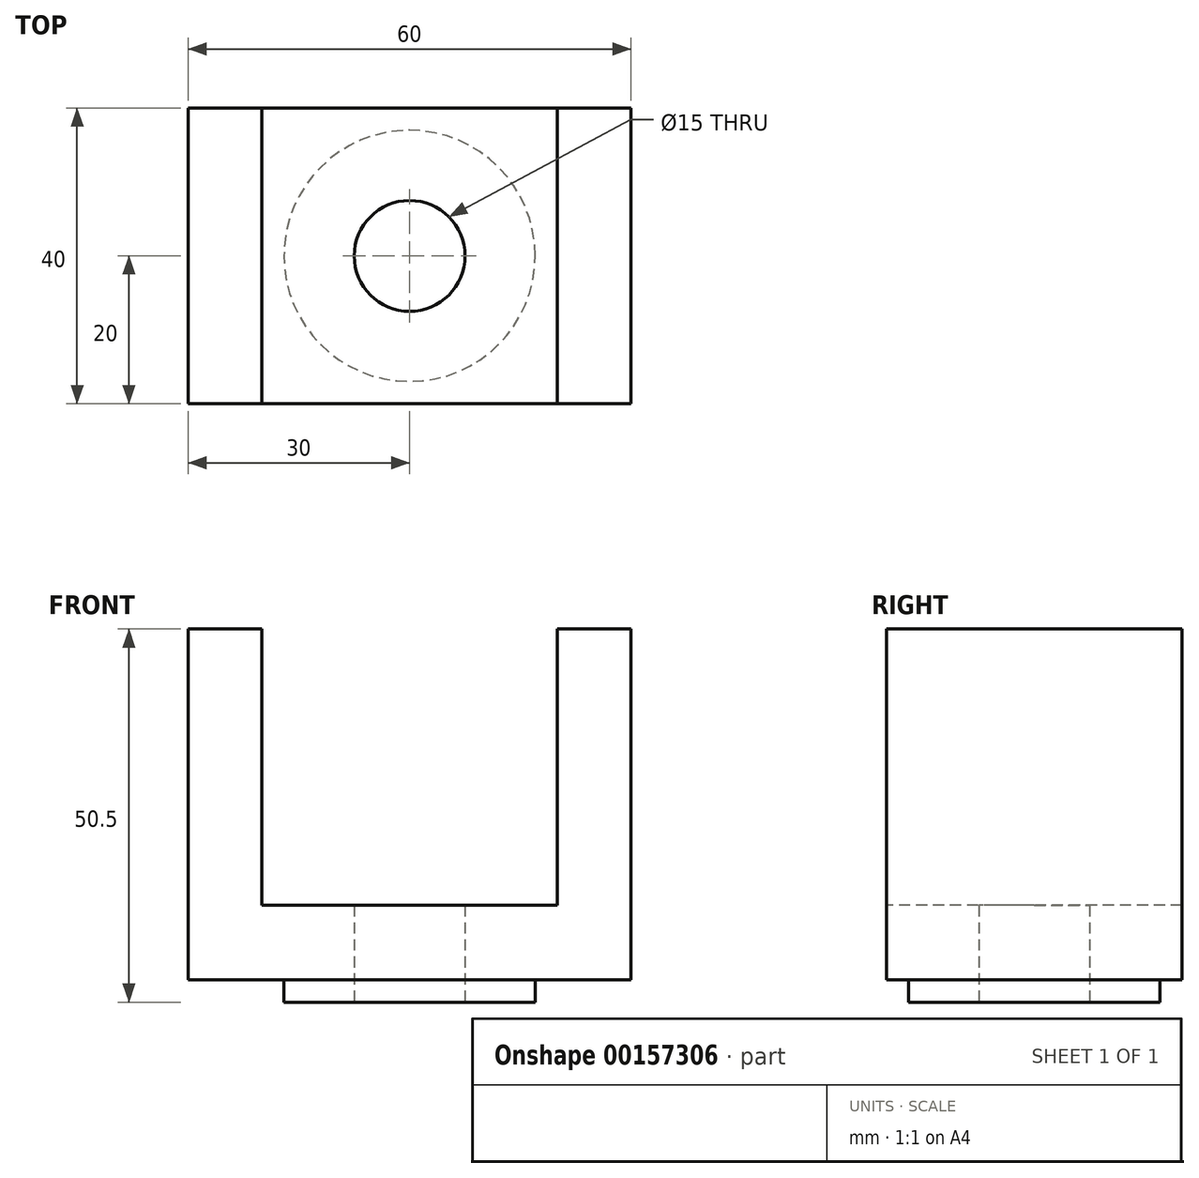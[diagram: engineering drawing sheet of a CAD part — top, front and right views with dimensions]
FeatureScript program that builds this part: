
annotation { "Feature Type Name" : "Feature", "Feature Type Description" : "" }
export const myFeature = defineFeature(function(context is Context, id is Id, definition is map)
    precondition{}
    {
        {
            var Q0;
            Q0=qCreatedBy(makeId("Top.planeOp"),FACE);
            var sketch = newSketch(context, id + "F0", { "sketchPlane" : qUnion([Q0])});
            skLineSegment(sketch, "E0", {"start": v(0, 0) * mm, "end": v(60, 0) * mm});
            skLineSegment(sketch, "E1", {"start": v(60, 0) * mm, "end": v(60, -40) * mm});
            skLineSegment(sketch, "E2", {"start": v(60, -40) * mm, "end": v(0, -40) * mm});
            skLineSegment(sketch, "E3", {"start": v(0, -40) * mm, "end": v(0, 0) * mm});
            skSolve(sketch);
        }
        {
            var Q0;
            Q0 = qSketchRegion(id + "F0", true);
            extrude(context, id + "F1", {"entities" : qUnion([Q0]), "depth" : 50.5 * mm});
        }
        {
            var Q0;
            Q0=makeQuery(id+"F1.opExtrude","SWEPT_FACE",FACE,{"disambiguationData":[OSD([sQuery(id+"F0.wireOp",EDGE,"E2")])]});
            var sketch = newSketch(context, id + "F2", { "sketchPlane" : qUnion([Q0])});
            skLineSegment(sketch, "E4", {"start": v(0, 0) * mm, "end": v(0, 3) * mm});
            skLineSegment(sketch, "E5", {"start": v(0, 3) * mm, "end": v(60, 3) * mm});
            skLineSegment(sketch, "E6", {"start": v(60, 3) * mm, "end": v(60, 0) * mm});
            skLineSegment(sketch, "E7", {"start": v(60, 0) * mm, "end": v(0, 0) * mm});
            skSolve(sketch);
        }
        {
            var Q0;
            Q0 = qSketchRegion(id + "F2", true);
            extrude(context, id + "F3", {"entities" : qUnion([Q0]), "operationType" : NewBodyOperationType.REMOVE, "endBound" : BoundingType.THROUGH_ALL, "oppositeDirection" : true, "depth" : 25 * mm});
        }
        {
            var Q0;
            Q0=makeQuery(id+"F3.boolean.opBoolean","COPY",FACE,{"derivedFrom":makeQuery(id+"F3.opExtrude","SWEPT_FACE",FACE,{"disambiguationData":[OSD([sQuery(id+"F2.wireOp",EDGE,"E5")])]})});
            var sketch = newSketch(context, id + "F4", { "sketchPlane" : qUnion([Q0])});
            skLineSegment(sketch, "E8", {"start": v(0, 0) * mm, "end": v(60, 0) * mm});
            skCircle(sketch, "E9", {"center": v(30, 20) * mm, "radius": 17 * mm});
            skSolve(sketch);
        }
        {
            var Q0;
            Q0 = qSketchRegion(id + "F4", true);
            extrude(context, id + "F5", {"entities" : qUnion([Q0]), "operationType" : NewBodyOperationType.ADD, "depth" : 3 * mm});
        }
        {
            var Q0;
            Q0=makeQuery(id+"F1.opExtrude","SWEPT_FACE",FACE,{"disambiguationData":[OSD([sQuery(id+"F0.wireOp",EDGE,"E2")])]});
            var sketch = newSketch(context, id + "F6", { "sketchPlane" : qUnion([Q0])});
            skLineSegment(sketch, "E10", {"start": v(0, 3) * mm, "end": v(0, 50.5) * mm});
            skLineSegment(sketch, "E11", {"start": v(0, 50.5) * mm, "end": v(10, 50.5) * mm});
            skLineSegment(sketch, "E12", {"start": v(10, 50.5) * mm, "end": v(10, 13.1) * mm});
            skLineSegment(sketch, "E13", {"start": v(50, 13.1) * mm, "end": v(50, 50.5) * mm});
            skLineSegment(sketch, "E14", {"start": v(50, 50.5) * mm, "end": v(60, 50.5) * mm});
            skLineSegment(sketch, "E15", {"start": v(50, 13.1) * mm, "end": v(10, 13.1) * mm});
            skLineSegment(sketch, "E16", {"start": v(60, 50.5) * mm, "end": v(60, 3) * mm});
            skLineSegment(sketch, "E17", {"start": v(60, 3) * mm, "end": v(0, 3) * mm});
            skSolve(sketch);
        }
        {
            var Q0;
            {var subQ0=sQuery(id+"F6.wireOp",EDGE,"E12");Q0=makeQuery(id+"F6.imprint","IMPRINT",FACE,{"disambiguationData":[TD([[makeQuery(id+"F6.imprint","IMPRINT",EDGE,{"derivedFrom":subQ0}),1.0]])]});}
            extrude(context, id + "F7", {"entities" : qUnion([Q0]), "operationType" : NewBodyOperationType.REMOVE, "endBound" : BoundingType.THROUGH_ALL, "oppositeDirection" : true, "depth" : 25 * mm});
        }
        {
            var Q0;
            Q0=makeQuery(id+"F5.opExtrude","CAP_FACE",FACE,{"disambiguationData":[OSD([sQuery(id+"F4.wireOp",EDGE,"E9")])],"isStart":false});
            var sketch = newSketch(context, id + "F8", { "sketchPlane" : qUnion([Q0])});
            skCircle(sketch, "E18", {"center": v(30, 20) * mm, "radius": 7.5 * mm});
            skSolve(sketch);
        }
        {
            var Q0;
            Q0 = qSketchRegion(id + "F8", true);
            extrude(context, id + "F9", {"entities" : qUnion([Q0]), "operationType" : NewBodyOperationType.REMOVE, "endBound" : BoundingType.THROUGH_ALL, "oppositeDirection" : true, "depth" : 25 * mm});
        }
    });
